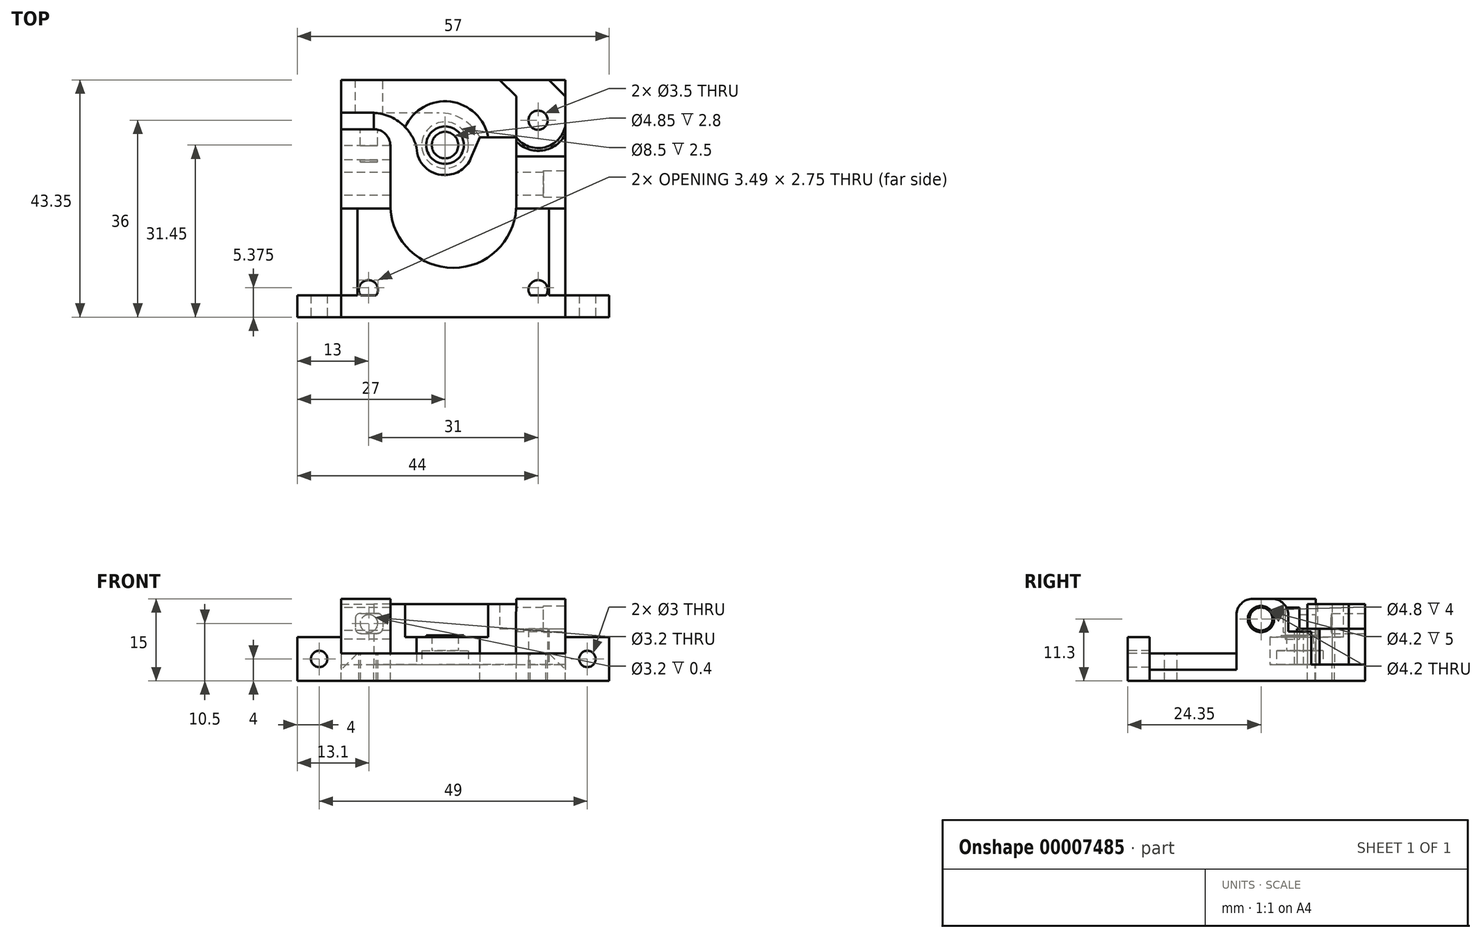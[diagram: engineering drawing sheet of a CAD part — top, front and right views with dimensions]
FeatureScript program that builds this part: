
annotation { "Feature Type Name" : "Feature", "Feature Type Description" : "" }
export const myFeature = defineFeature(function(context is Context, id is Id, definition is map)
    precondition{}
    {
        {
            var Q0;
            Q0=qCreatedBy(makeId("Top.planeOp"),FACE);
            var sketch = newSketch(context, id + "F0", { "sketchPlane" : qUnion([Q0])});
            skLineSegment(sketch, "E0.bottom", {"start": v(-15.5, 15.5) * mm, "end": v(15.5, 15.5) * mm, "construction": true});
            skLineSegment(sketch, "E0.top", {"start": v(-15.5, -15.5) * mm, "end": v(15.5, -15.5) * mm, "construction": true});
            skLineSegment(sketch, "E0.left", {"start": v(-15.5, 15.5) * mm, "end": v(-15.5, -15.5) * mm, "construction": true});
            skLineSegment(sketch, "E0.right", {"start": v(15.5, 15.5) * mm, "end": v(15.5, -15.5) * mm, "construction": true});
            skCircle(sketch, "E1", {"center": v(0, 0) * mm, "radius": 11.5 * mm});
            skLineSegment(sketch, "E2", {"start": v(-15.5, 0) * mm, "end": v(0, 0) * mm, "construction": true});
            skLineSegment(sketch, "E3", {"start": v(0, 0) * mm, "end": v(0, 15.5) * mm, "construction": true});
            skLineSegment(sketch, "E4.0", {"start": v(-20.5, 20.5) * mm, "end": v(20.5, 20.5) * mm});
            skLineSegment(sketch, "E4.1", {"start": v(-20.5, 20.5) * mm, "end": v(-20.5, -20.5) * mm});
            skLineSegment(sketch, "E4.2", {"start": v(-20.5, -20.5) * mm, "end": v(20.5, -20.5) * mm});
            skLineSegment(sketch, "E4.3", {"start": v(20.5, 20.5) * mm, "end": v(20.5, -20.5) * mm});
            skCircle(sketch, "E5", {"center": v(15.5, 15.5) * mm, "radius": 1.75 * mm});
            skCircle(sketch, "E6", {"center": v(-15.5, -15.5) * mm, "radius": 1.75 * mm});
            skCircle(sketch, "E7", {"center": v(15.5, -15.5) * mm, "radius": 1.75 * mm});
            skCircle(sketch, "E8", {"center": v(0, 0) * mm, "radius": 3.75 * mm, "construction": true});
            skCircle(sketch, "E9", {"center": v(-1.5, 10.95) * mm, "radius": 7 * mm, "construction": true});
            skLineSegment(sketch, "E10", {"start": v(0, 3.85) * mm, "end": v(-20.5, 3.85) * mm, "construction": true});
            skLineSegment(sketch, "E11.bottom", {"start": v(-11.5, 0) * mm, "end": v(11.5, 0) * mm, "construction": true});
            skLineSegment(sketch, "E11.left", {"start": v(-11.5, 0) * mm, "end": v(-11.5, 10.85) * mm});
            skLineSegment(sketch, "E11.right", {"start": v(11.5, 0) * mm, "end": v(11.5, 8.85) * mm});
            skLineSegment(sketch, "E12", {"start": v(-20.5, 13.85) * mm, "end": v(-14.5, 13.85) * mm});
            skLineSegment(sketch, "E13", {"start": v(11.5, 8.85) * mm, "end": v(20.5, 8.85) * mm});
            skCircle(sketch, "E14", {"center": v(-1.5, 10.95) * mm, "radius": 2.43 * mm});
            skLineSegment(sketch, "E15", {"start": v(-20.5, 16.85) * mm, "end": v(-2.6, 16.85) * mm});
            skLineSegment(sketch, "E16", {"start": v(-20.5, 22.85) * mm, "end": v(20.5, 22.85) * mm});
            skLineSegment(sketch, "E17", {"start": v(-15.5, 0) * mm, "end": v(-20.5, 0) * mm});
            skLineSegment(sketch, "E18", {"start": v(20.5, 0) * mm, "end": v(11.5, 0) * mm});
            skLineSegment(sketch, "E19", {"start": v(-15.5, 0) * mm, "end": v(-11.5, 0) * mm});
            skLineSegment(sketch, "E20", {"start": v(11.5, 8.85) * mm, "end": v(11.5, 12.35) * mm});
            skLineSegment(sketch, "E21", {"start": v(-11.48, -0.65) * mm, "end": v(-20.5, -0.65) * mm});
            skLineSegment(sketch, "E22", {"start": v(11.48, -0.65) * mm, "end": v(20.5, -0.65) * mm});
            skCircle(sketch, "E23", {"center": v(-1.5, 10.95) * mm, "radius": 1.5 * mm});
            skLineSegment(sketch, "E24", {"start": v(-1.68, 5.5) * mm, "end": v(-1.37, 5.5) * mm});
            skLineSegment(sketch, "E25", {"start": v(3.23, 8.53) * mm, "end": v(4.86, 12.35) * mm});
            skPoint(sketch, "E26.visualSharp", {"position": v(-6.13, 5.5) * mm});
            skArc(sketch, "E26.filletArc", {"start": v(-6.68, 10.44) * mm, "mid": v(-5.2, 6.94) * mm, "end": v(-1.68, 5.5) * mm});
            skPoint(sketch, "E27.visualSharp", {"position": v(1.93, 5.5) * mm});
            skArc(sketch, "E27.filletArc", {"start": v(-1.37, 5.5) * mm, "mid": v(1.38, 6.33) * mm, "end": v(3.23, 8.53) * mm});
            skPoint(sketch, "E28.visualSharp", {"position": v(-11.5, 13.85) * mm});
            skArc(sketch, "E28.filletArc", {"start": v(-11.5, 10.85) * mm, "mid": v(-12.38, 12.97) * mm, "end": v(-14.5, 13.85) * mm});
            skLineSegment(sketch, "E29", {"start": v(11.5, 12.35) * mm, "end": v(4.86, 12.35) * mm});
            skLineSegment(sketch, "E30", {"start": v(20.5, 20.5) * mm, "end": v(20.5, 22.85) * mm});
            skLineSegment(sketch, "E31", {"start": v(-20.5, 20.5) * mm, "end": v(-20.5, 22.85) * mm});
            skLineSegment(sketch, "E32", {"start": v(-14.5, 13.85) * mm, "end": v(-14.5, 16.85) * mm});
            skArc(sketch, "E33", {"start": v(11.5, 12.35) * mm, "mid": v(16.7, 10.55) * mm, "end": v(20.5, 14.54) * mm});
            skArc(sketch, "E34.0", {"start": v(11.5, 11.6) * mm, "mid": v(16.36, 9.97) * mm, "end": v(20.5, 13) * mm});
            skArc(sketch, "E35", {"start": v(-6.68, 10.44) * mm, "mid": v(-9.54, 14.93) * mm, "end": v(-14.5, 16.85) * mm});
            skArc(sketch, "E36", {"start": v(4.86, 12.35) * mm, "mid": v(1.76, 15.64) * mm, "end": v(-2.6, 16.85) * mm});
            skSolve(sketch);
        }
        {
            var Q0;
            {var subQ11=sQuery(id+"F0.wireOp",EDGE,"E4.0");Q0=makeQuery(id+"F0.imprint","IMPRINT",FACE,{"disambiguationData":[TD([[makeQuery(id+"F0.imprint","IMPRINT",EDGE,{"derivedFrom":subQ11}),-1.0]])]});}
            var Q1;
            Q1=makeQuery(id+"F0.imprint","IMPRINT",FACE,{"disambiguationData":[TD([[makeQuery(id+"F0.imprint","IMPRINT",EDGE,{"derivedFrom":sQuery(id+"F0.wireOp",EDGE,"E11.right")}),-1.0]])]});
            var Q2;
            {var subQ3=sQuery(id+"F0.wireOp",EDGE,"E4.2");Q2=makeQuery(id+"F0.imprint","IMPRINT",FACE,{"disambiguationData":[TD([[makeQuery(id+"F0.imprint","IMPRINT",EDGE,{"derivedFrom":subQ3}),1.0]])]});}
            var Q3;
            Q3=makeQuery(id+"F0.imprint","IMPRINT",FACE,{"disambiguationData":[TD([[makeQuery(id+"F0.imprint","IMPRINT",EDGE,{"derivedFrom":sQuery(id+"F0.wireOp",EDGE,"E11.left")}),1.0]])]});
            var Q4;
            {var subQ1=sQuery(id+"F0.wireOp",EDGE,"E18");Q4=makeQuery(id+"F0.imprint","IMPRINT",FACE,{"disambiguationData":[TD([[makeQuery(id+"F0.imprint","IMPRINT",EDGE,{"derivedFrom":subQ1}),1.0]])]});}
            var Q5;
            {var subQ2=sQuery(id+"F0.wireOp",EDGE,"E17");Q5=makeQuery(id+"F0.imprint","IMPRINT",FACE,{"disambiguationData":[TD([[makeQuery(id+"F0.imprint","IMPRINT",EDGE,{"derivedFrom":subQ2}),1.0]])]});}
            var Q6;
            {var subQ11=sQuery(id+"F0.wireOp",EDGE,"E4.0");Q6=makeQuery(id+"F0.imprint","IMPRINT",FACE,{"disambiguationData":[TD([[makeQuery(id+"F0.imprint","IMPRINT",EDGE,{"derivedFrom":subQ11}),-1.0]])]});}
            var Q7;
            Q7=makeQuery(id+"F0.imprint","IMPRINT",FACE,{"disambiguationData":[TD([[makeQuery(id+"F0.imprint","IMPRINT",EDGE,{"derivedFrom":sQuery(id+"F0.wireOp",EDGE,"E4.0")}),1.0]])]});
            var Q8;
            {var subQ4=sQuery(id+"F0.wireOp",EDGE,"E12");Q8=makeQuery(id+"F0.imprint","IMPRINT",FACE,{"disambiguationData":[TD([[makeQuery(id+"F0.imprint","IMPRINT",EDGE,{"derivedFrom":subQ4}),1.0]])]});}
            var Q9;
            {var subQ2=sQuery(id+"F0.wireOp",EDGE,"E13");Q9=makeQuery(id+"F0.imprint","IMPRINT",FACE,{"disambiguationData":[TD([[makeQuery(id+"F0.imprint","IMPRINT",EDGE,{"derivedFrom":subQ2}),1.0]])]});}
            var Q10;
            {var subQ1=sQuery(id+"F0.wireOp",EDGE,"E33");Q10=makeQuery(id+"F0.imprint","IMPRINT",FACE,{"disambiguationData":[TD([[makeQuery(id+"F0.imprint","IMPRINT",EDGE,{"derivedFrom":subQ1}),-1.0]])]});}
            extrude(context, id + "F1", {"entities" : qUnion([Q0, Q1, Q2, Q3, Q4, Q5, Q6, Q7, Q8, Q9, Q10]), "oppositeDirection" : true, "depth" : 3 * mm});
        }
        {
            var Q0;
            {var subQ1=sQuery(id+"F0.wireOp",EDGE,"97cd7f3d-8e90-465d-8939-76c9784581d8");Q0=makeQuery(id+"F0.imprint","IMPRINT",FACE,{"disambiguationData":[TD([[makeQuery(id+"F0.imprint","IMPRINT",EDGE,{"derivedFrom":subQ1}),1.0]])]});}
            var Q1;
            {var subQ6=sQuery(id+"F0.wireOp",EDGE,"E4.0");Q1=makeQuery(id+"F0.imprint","IMPRINT",FACE,{"disambiguationData":[TD([[makeQuery(id+"F0.imprint","IMPRINT",EDGE,{"derivedFrom":subQ6}),-1.0]])]});}
            var Q2;
            Q2=makeQuery(id+"F0.imprint","IMPRINT",FACE,{"disambiguationData":[TD([[makeQuery(id+"F0.imprint","IMPRINT",EDGE,{"derivedFrom":sQuery(id+"F0.wireOp",EDGE,"E4.0")}),1.0]])]});
            var Q3;
            {var subQ1=sQuery(id+"F0.wireOp",EDGE,"E1");var subQ5=sQuery(id+"F0.wireOp",EDGE,"E14");var subQ7=makeQuery(id+"F0.imprint","INTERSECT",VERTEX,{"disambiguationData":[OD(1.0)],"derivedFrom":[subQ1,subQ5]});Q3=makeQuery(id+"F0.imprint","IMPRINT",FACE,{"disambiguationData":[TD([[makeQuery(id+"F0.imprint","IMPRINT",EDGE,{"disambiguationData":[TD([[subQ7,-1.0]])],"derivedFrom":subQ1}),1.0]])]});}
            var Q4;
            {var subQ0=sQuery(id+"F0.wireOp",EDGE,"E27.filletArc");Q4=makeQuery(id+"F0.imprint","IMPRINT",FACE,{"disambiguationData":[TD([[makeQuery(id+"F0.imprint","IMPRINT",EDGE,{"derivedFrom":subQ0}),1.0]])]});}
            var Q5;
            {var subQ4=sQuery(id+"F0.wireOp",EDGE,"E35");Q5=makeQuery(id+"F0.imprint","IMPRINT",FACE,{"disambiguationData":[TD([[makeQuery(id+"F0.imprint","IMPRINT",EDGE,{"derivedFrom":subQ4}),-1.0]])]});}
            extrude(context, id + "F2", {"entities" : qUnion([Q0, Q1, Q2, Q3, Q4, Q5]), "depth" : 10 * mm});
        }
        {
            var Q0;
            Q0=makeQuery(id+"F0.imprint","IMPRINT",FACE,{"disambiguationData":[TD([[makeQuery(id+"F0.imprint","IMPRINT",EDGE,{"derivedFrom":sQuery(id+"F0.wireOp",EDGE,"E11.right")}),-1.0]])]});
            var Q1;
            {var subQ1=sQuery(id+"F0.wireOp",EDGE,"E18");Q1=makeQuery(id+"F0.imprint","IMPRINT",FACE,{"disambiguationData":[TD([[makeQuery(id+"F0.imprint","IMPRINT",EDGE,{"derivedFrom":subQ1}),1.0]])]});}
            var Q2;
            {var subQ2=sQuery(id+"F0.wireOp",EDGE,"E17");Q2=makeQuery(id+"F0.imprint","IMPRINT",FACE,{"disambiguationData":[TD([[makeQuery(id+"F0.imprint","IMPRINT",EDGE,{"derivedFrom":subQ2}),1.0]])]});}
            var Q3;
            Q3=makeQuery(id+"F0.imprint","IMPRINT",FACE,{"disambiguationData":[TD([[makeQuery(id+"F0.imprint","IMPRINT",EDGE,{"derivedFrom":sQuery(id+"F0.wireOp",EDGE,"E11.left")}),1.0]])]});
            var Q4;
            Q4=makeQuery(id+"F2.opExtrude","CAP_FACE",FACE,{"disambiguationData":[OSD([sQuery(id+"F0.wireOp",EDGE,"E4.1"),sQuery(id+"F0.wireOp",EDGE,"E4.3"),sQuery(id+"F0.wireOp",EDGE,"E5"),sQuery(id+"F0.wireOp",EDGE,"E14"),sQuery(id+"F0.wireOp",EDGE,"E15"),sQuery(id+"F0.wireOp",EDGE,"E16"),sQuery(id+"F0.wireOp",EDGE,"4d0ce63a-1545-49a6-93f2-0e6cf358bf14"),sQuery(id+"F0.wireOp",EDGE,"E24"),sQuery(id+"F0.wireOp",EDGE,"E25"),sQuery(id+"F0.wireOp",EDGE,"E26.filletArc"),sQuery(id+"F0.wireOp",EDGE,"E27.filletArc"),sQuery(id+"F0.wireOp",EDGE,"E29"),sQuery(id+"F0.wireOp",EDGE,"E30"),sQuery(id+"F0.wireOp",EDGE,"E31"),sQuery(id+"F0.wireOp",EDGE,"E33")])],"isStart":false});
            extrude(context, id + "F3", {"entities" : qUnion([Q0, Q1, Q2, Q3]), "operationType" : NewBodyOperationType.ADD, "endBoundEntity" : qUnion([Q4]), "depth" : 12 * mm});
        }
        {
            var Q0;
            Q0=makeQuery(id+"F2.opExtrude","CAP_FACE",FACE,{"disambiguationData":[OSD([sQuery(id+"F0.wireOp",EDGE,"E4.1"),sQuery(id+"F0.wireOp",EDGE,"E4.3"),sQuery(id+"F0.wireOp",EDGE,"E5"),sQuery(id+"F0.wireOp",EDGE,"E14"),sQuery(id+"F0.wireOp",EDGE,"E15"),sQuery(id+"F0.wireOp",EDGE,"E16"),sQuery(id+"F0.wireOp",EDGE,"4d0ce63a-1545-49a6-93f2-0e6cf358bf14"),sQuery(id+"F0.wireOp",EDGE,"E24"),sQuery(id+"F0.wireOp",EDGE,"E25"),sQuery(id+"F0.wireOp",EDGE,"E26.filletArc"),sQuery(id+"F0.wireOp",EDGE,"E27.filletArc"),sQuery(id+"F0.wireOp",EDGE,"E29"),sQuery(id+"F0.wireOp",EDGE,"E30"),sQuery(id+"F0.wireOp",EDGE,"E31"),sQuery(id+"F0.wireOp",EDGE,"E33")])],"isStart":false});
            var sketch = newSketch(context, id + "F4", { "sketchPlane" : qUnion([Q0])});
            skLineSegment(sketch, "E37.0", {"start": v(11.5, 8.85) * mm, "end": v(20.5, 8.85) * mm});
            skCircle(sketch, "E38.0", {"center": v(-1.5, 10.95) * mm, "radius": 7 * mm});
            skCircle(sketch, "E38.1", {"center": v(-1.5, 10.95) * mm, "radius": 2.43 * mm});
            skCircle(sketch, "E39.0", {"center": v(-1.5, 10.95) * mm, "radius": 8 * mm});
            skSolve(sketch);
        }
        {
            var Q0;
            Q0=makeQuery(id+"F4.imprint","IMPRINT",FACE,{"disambiguationData":[TD([[makeQuery(id+"F4.imprint","IMPRINT",EDGE,{"derivedFrom":sQuery(id+"F4.wireOp",EDGE,"E38.1")}),-1.0]])]});
            var Q1;
            {var subQ0=makeQuery(id+"F2.opExtrude","CAP_EDGE",EDGE,{"disambiguationData":[OSD([sQuery(id+"F0.wireOp",EDGE,"E16")])],"isStart":false});var subQ1=sQuery(id+"F4.wireOp",EDGE,"E38.0");var subQ2=makeQuery(id+"F4.imprint","INTERSECT",VERTEX,{"disambiguationData":[OD(1.0)],"derivedFrom":[subQ0,subQ1]});Q1=makeQuery(id+"F4.imprint","IMPRINT",FACE,{"disambiguationData":[TD([[makeQuery(id+"F4.imprint","IMPRINT",EDGE,{"disambiguationData":[TD([[subQ2,1.0]])],"derivedFrom":subQ1}),-1.0]])]});}
            var Q2;
            {var subQ0=makeQuery(id+"F2.opExtrude","CAP_EDGE",EDGE,{"disambiguationData":[OSD([sQuery(id+"F0.wireOp",EDGE,"E16")])],"isStart":false});var subQ1=sQuery(id+"F4.wireOp",EDGE,"E38.0");var subQ2=makeQuery(id+"F4.imprint","INTERSECT",VERTEX,{"disambiguationData":[OD(0.0)],"derivedFrom":[subQ0,subQ1]});Q2=makeQuery(id+"F4.imprint","IMPRINT",FACE,{"disambiguationData":[TD([[makeQuery(id+"F4.imprint","IMPRINT",EDGE,{"disambiguationData":[TD([[subQ2,-1.0]])],"derivedFrom":subQ1}),-1.0]])]});}
            extrude(context, id + "F5", {"entities" : qUnion([Q0, Q1, Q2]), "operationType" : NewBodyOperationType.REMOVE, "oppositeDirection" : true, "depth" : 5 * mm});
        }
        {
            var Q0;
            {var subQ0=sQuery(id+"F0.wireOp",EDGE,"E4.3");Q0=makeQuery(id+"F2.boolean.opBoolean","MERGE",FACE,{"derivedFrom":[makeQuery(id+"F1.opExtrude","SWEPT_FACE",FACE,{"disambiguationData":[OSD([subQ0])]}),makeQuery(id+"F2.opExtrude","SWEPT_FACE",FACE,{"disambiguationData":[OSD([subQ0])]})]});}
            var sketch = newSketch(context, id + "F6", { "sketchPlane" : qUnion([Q0])});
            skCircle(sketch, "E40", {"center": v(3.85, 8.3) * mm, "radius": 1.5 * mm});
            skPoint(sketch, "E41.0", {"position": v(3.85, 0) * mm});
            skLineSegment(sketch, "E42.0", {"start": v(8.53, 5) * mm, "end": v(13.38, 5) * mm});
            skSolve(sketch);
        }
        {
            var Q0;
            Q0=makeQuery(id+"F6.imprint","IMPRINT",FACE,{"disambiguationData":[TD([[makeQuery(id+"F6.imprint","IMPRINT",EDGE,{"derivedFrom":sQuery(id+"F6.wireOp",EDGE,"E40")}),1.0]])]});
            extrude(context, id + "F7", {"entities" : qUnion([Q0]), "operationType" : NewBodyOperationType.REMOVE, "oppositeDirection" : true, "depth" : 50 * mm});
        }
        {
            var Q0;
            Q0=makeQuery(id+"F2.opExtrude","SWEPT_FACE",FACE,{"disambiguationData":[OSD([sQuery(id+"F0.wireOp",EDGE,"E16")])]});
            var sketch = newSketch(context, id + "F8", { "sketchPlane" : qUnion([Q0])});
            skLineSegment(sketch, "E43", {"start": v(15.4, 10) * mm, "end": v(15.4, 7.5) * mm, "construction": true});
            skCircle(sketch, "E44", {"center": v(15.4, 7.5) * mm, "radius": 1.6 * mm});
            skLineSegment(sketch, "E45.0", {"start": v(-0.93, 5) * mm, "end": v(3.92, 5) * mm, "construction": true});
            skLineSegment(sketch, "E46", {"start": v(3.92, 5) * mm, "end": v(3.92, 10) * mm, "construction": true});
            skLineSegment(sketch, "E47", {"start": v(3.92, 10) * mm, "end": v(3.92, 7.5) * mm, "construction": true});
            skLineSegment(sketch, "E48", {"start": v(3.92, 7.5) * mm, "end": v(15.4, 7.5) * mm, "construction": true});
            skSolve(sketch);
        }
        {
            var Q0;
            Q0=makeQuery(id+"F8.imprint","IMPRINT",FACE,{"disambiguationData":[TD([[makeQuery(id+"F8.imprint","IMPRINT",EDGE,{"derivedFrom":sQuery(id+"F8.wireOp",EDGE,"E44")}),1.0]])]});
            var Q1;
            Q1=sQuery(id+"F8.wireOp",EDGE,"E44");
            extrude(context, id + "F9", {"entities" : qUnion([Q0]), "operationType" : NewBodyOperationType.REMOVE, "surfaceEntities" : qUnion([Q1]), "oppositeDirection" : true, "depth" : 15 * mm});
        }
        {
            var Q0;
            {var subQ0=sQuery(id+"F0.wireOp",EDGE,"E4.1");var subQ1=makeQuery(id+"F0.imprint","INTERSECT",VERTEX,{"derivedFrom":[subQ0,sQuery(id+"F0.wireOp",EDGE,"E17")]});var subQ2=makeQuery(id+"F0.imprint","IMPRINT",EDGE,{"disambiguationData":[TD([[makeQuery(id+"F0.imprint","INTERSECT",VERTEX,{"derivedFrom":[subQ0,sQuery(id+"F0.wireOp",EDGE,"E12")]}),-1.0]])],"derivedFrom":subQ0});var subQ4=makeQuery(id+"F0.imprint","IMPRINT",EDGE,{"disambiguationData":[TD([[subQ1,-1.0]])],"derivedFrom":subQ0});Q0=makeQuery(id+"F2.boolean.opBoolean","MERGE",FACE,{"derivedFrom":[makeQuery(id+"F1.opExtrude","SWEPT_FACE",FACE,{"disambiguationData":[OSD([subQ0]),TDD([subQ2,subQ4,makeQuery(id+"F0.imprint","IMPRINT",EDGE,{"disambiguationData":[TD([[makeQuery(id+"F0.imprint","INTERSECT",VERTEX,{"derivedFrom":[subQ0,sQuery(id+"F0.wireOp",EDGE,"E4.2")]}),1.0]])],"derivedFrom":subQ0})])]}),makeQuery(id+"F2.opExtrude","SWEPT_FACE",FACE,{"disambiguationData":[OSD([subQ0]),TDD([subQ2,subQ4])]})]});}
            var sketch = newSketch(context, id + "F10", { "sketchPlane" : qUnion([Q0])});
            skLineSegment(sketch, "E49", {"start": v(-22.85, 7.5) * mm, "end": v(-9.55, 7.5) * mm});
            skLineSegment(sketch, "E50.rect.bottom", {"start": v(-8.25, 10.4) * mm, "end": v(-10.85, 10.4) * mm});
            skLineSegment(sketch, "E50.rect.top", {"start": v(-8.25, 4.6) * mm, "end": v(-10.85, 4.6) * mm});
            skLineSegment(sketch, "E50.rect.left", {"start": v(-8.25, 10.4) * mm, "end": v(-8.25, 4.6) * mm});
            skLineSegment(sketch, "E50.rect.right", {"start": v(-10.85, 10.4) * mm, "end": v(-10.85, 4.6) * mm});
            skPoint(sketch, "E50.rect.middle", {"position": v(-9.55, 7.5) * mm});
            skLineSegment(sketch, "E51.0", {"start": v(-22.85, 5.9) * mm, "end": v(-22.85, 9.1) * mm});
            skSolve(sketch);
        }
        {
            var Q0;
            {var subQ3=sQuery(id+"F10.wireOp",EDGE,"E50.rect.bottom");Q0=makeQuery(id+"F10.imprint","IMPRINT",FACE,{"disambiguationData":[TD([[makeQuery(id+"F10.imprint","IMPRINT",EDGE,{"derivedFrom":subQ3}),1.0]])]});}
            extrude(context, id + "F11", {"entities" : qUnion([Q0]), "operationType" : NewBodyOperationType.REMOVE, "oppositeDirection" : true, "depth" : 9 * mm});
        }
        {
            var Q0;
            Q0=makeQuery(id+"F2.opExtrude","SWEPT_FACE",FACE,{"disambiguationData":[OSD([sQuery(id+"F0.wireOp",EDGE,"E16")])]});
            var sketch = newSketch(context, id + "F12", { "sketchPlane" : qUnion([Q0])});
            skCircle(sketch, "E52.0", {"center": v(15.4, 7.5) * mm, "radius": 1.6 * mm});
            skLineSegment(sketch, "E53.rect.bottom", {"start": v(16.9, 9.34) * mm, "end": v(13.9, 9.34) * mm});
            skLineSegment(sketch, "E53.rect.top", {"start": v(16.9, 5.66) * mm, "end": v(13.9, 5.66) * mm});
            skLineSegment(sketch, "E53.rect.left", {"start": v(17.9, 8.34) * mm, "end": v(17.9, 6.66) * mm});
            skLineSegment(sketch, "E53.rect.right", {"start": v(12.9, 8.34) * mm, "end": v(12.9, 6.66) * mm});
            skPoint(sketch, "E54.visualSharp", {"position": v(17.9, 9.34) * mm});
            skArc(sketch, "E54.filletArc", {"start": v(17.9, 8.34) * mm, "mid": v(17.62, 9.05) * mm, "end": v(16.9, 9.34) * mm});
            skPoint(sketch, "E55.visualSharp", {"position": v(17.9, 5.66) * mm});
            skArc(sketch, "E55.filletArc", {"start": v(16.9, 5.66) * mm, "mid": v(17.62, 5.95) * mm, "end": v(17.9, 6.66) * mm});
            skPoint(sketch, "E56.visualSharp", {"position": v(12.9, 5.66) * mm});
            skArc(sketch, "E56.filletArc", {"start": v(12.9, 6.66) * mm, "mid": v(13.18, 5.95) * mm, "end": v(13.9, 5.66) * mm});
            skPoint(sketch, "E57.visualSharp", {"position": v(12.9, 9.34) * mm});
            skArc(sketch, "E57.filletArc", {"start": v(13.9, 9.34) * mm, "mid": v(13.18, 9.05) * mm, "end": v(12.9, 8.34) * mm});
            skSolve(sketch);
        }
        {
            var Q0;
            Q0=makeQuery(id+"F12.imprint","IMPRINT",FACE,{"disambiguationData":[TD([[makeQuery(id+"F12.imprint","IMPRINT",EDGE,{"derivedFrom":sQuery(id+"F12.wireOp",EDGE,"E52.0")}),-1.0]])]});
            extrude(context, id + "F13", {"entities" : qUnion([Q0]), "operationType" : NewBodyOperationType.REMOVE, "endBound" : BoundingType.UP_TO_NEXT, "oppositeDirection" : true, "depth" : 5 * mm});
        }
        {
            var Q0;
            {var subQ0=sQuery(id+"F0.wireOp",EDGE,"E4.3");Q0=makeQuery(id+"F2.boolean.opBoolean","MERGE",FACE,{"derivedFrom":[makeQuery(id+"F1.opExtrude","SWEPT_FACE",FACE,{"disambiguationData":[OSD([subQ0])]}),makeQuery(id+"F2.opExtrude","SWEPT_FACE",FACE,{"disambiguationData":[OSD([subQ0])]})]});}
            var sketch = newSketch(context, id + "F14", { "sketchPlane" : qUnion([Q0])});
            skCircle(sketch, "E58.0", {"center": v(3.85, 8.3) * mm, "radius": 1.5 * mm});
            skCircle(sketch, "E59", {"center": v(3.85, 8.3) * mm, "radius": 2.4 * mm});
            skSolve(sketch);
        }
        {
            var Q0;
            Q0=makeQuery(id+"F14.imprint","IMPRINT",FACE,{"disambiguationData":[TD([[makeQuery(id+"F14.imprint","IMPRINT",EDGE,{"derivedFrom":sQuery(id+"F14.wireOp",EDGE,"E58.0")}),-1.0]])]});
            extrude(context, id + "F15", {"entities" : qUnion([Q0]), "operationType" : NewBodyOperationType.REMOVE, "oppositeDirection" : true, "depth" : 4 * mm});
        }
        {
            var Q0;
            {var subQ0=sQuery(id+"F0.wireOp",EDGE,"E4.1");var subQ1=makeQuery(id+"F0.imprint","INTERSECT",VERTEX,{"derivedFrom":[subQ0,sQuery(id+"F0.wireOp",EDGE,"E17")]});var subQ2=makeQuery(id+"F0.imprint","IMPRINT",EDGE,{"disambiguationData":[TD([[makeQuery(id+"F0.imprint","INTERSECT",VERTEX,{"derivedFrom":[subQ0,sQuery(id+"F0.wireOp",EDGE,"E12")]}),-1.0]])],"derivedFrom":subQ0});var subQ4=makeQuery(id+"F0.imprint","IMPRINT",EDGE,{"disambiguationData":[TD([[subQ1,-1.0]])],"derivedFrom":subQ0});Q0=makeQuery(id+"F2.boolean.opBoolean","MERGE",FACE,{"derivedFrom":[makeQuery(id+"F1.opExtrude","SWEPT_FACE",FACE,{"disambiguationData":[OSD([subQ0]),TDD([subQ2,subQ4,makeQuery(id+"F0.imprint","IMPRINT",EDGE,{"disambiguationData":[TD([[makeQuery(id+"F0.imprint","INTERSECT",VERTEX,{"derivedFrom":[subQ0,sQuery(id+"F0.wireOp",EDGE,"E4.2")]}),1.0]])],"derivedFrom":subQ0})])]}),makeQuery(id+"F2.opExtrude","SWEPT_FACE",FACE,{"disambiguationData":[OSD([subQ0]),TDD([subQ2,subQ4])]})]});}
            var sketch = newSketch(context, id + "F16", { "sketchPlane" : qUnion([Q0])});
            skCircle(sketch, "E60.0", {"center": v(-3.85, 8.3) * mm, "radius": 1.5 * mm});
            skCircle(sketch, "E61", {"center": v(-3.85, 8.3) * mm, "radius": 2.1 * mm});
            skSolve(sketch);
        }
        {
            var Q0;
            Q0=makeQuery(id+"F16.imprint","IMPRINT",FACE,{"disambiguationData":[TD([[makeQuery(id+"F16.imprint","IMPRINT",EDGE,{"derivedFrom":sQuery(id+"F16.wireOp",EDGE,"E60.0")}),-1.0]])]});
            var Q1;
            Q1=sQuery(id+"F16.wireOp",EDGE,"E61");
            extrude(context, id + "F17", {"entities" : qUnion([Q0]), "operationType" : NewBodyOperationType.REMOVE, "surfaceEntities" : qUnion([Q1]), "oppositeDirection" : true, "depth" : 46.76 * mm});
        }
        {
            var Q0;
            {var subQ0=sQuery(id+"F0.wireOp",EDGE,"E4.0");var subQ1=sQuery(id+"F0.wireOp",EDGE,"E15");var subQ2=sQuery(id+"F0.wireOp",EDGE,"4d0ce63a-1545-49a6-93f2-0e6cf358bf14");var subQ3=sQuery(id+"F0.wireOp",EDGE,"E24");var subQ4=sQuery(id+"F0.wireOp",EDGE,"E25");var subQ5=sQuery(id+"F0.wireOp",EDGE,"E26.filletArc");var subQ6=sQuery(id+"F0.wireOp",EDGE,"E27.filletArc");var subQ7=sQuery(id+"F4.wireOp",EDGE,"E38.0");var subQ8=sQuery(id+"F4.wireOp",EDGE,"E38.1");var subQ9=sQuery(id+"F4.wireOp",EDGE,"E39.0");Q0=makeQuery(id+"FuloRg8u4kZyhOY_7.boolean.opBoolean","MERGE",FACE,{"derivedFrom":[makeQuery(id+"F5.boolean.opBoolean","COPY",FACE,{"derivedFrom":makeQuery(id+"F5.opExtrude","CAP_FACE",FACE,{"disambiguationData":[OSD([subQ0,subQ1,subQ2,subQ3,subQ4,subQ5,subQ6,subQ7,subQ8,subQ9])],"isStart":false})}),makeQuery(id+"FuloRg8u4kZyhOY_7.opExtrude","SWEPT_FACE",FACE,{"disambiguationData":[OSD([subQ0,subQ1,subQ2,subQ3,subQ4,subQ5,subQ6,subQ7,subQ8,subQ9])]})]});}
            var sketch = newSketch(context, id + "F18", { "sketchPlane" : qUnion([Q0])});
            skCircle(sketch, "E62.0", {"center": v(-1.5, 10.95) * mm, "radius": 3.43 * mm});
            skSolve(sketch);
        }
        {
            var Q0;
            Q0=makeQuery(id+"F18.imprint","IMPRINT",FACE,{"disambiguationData":[TD([[makeQuery(id+"F18.imprint","IMPRINT",EDGE,{"derivedFrom":sQuery(id+"F18.wireOp",EDGE,"E62.0")}),1.0]])]});
            extrude(context, id + "F19", {"entities" : qUnion([Q0]), "operationType" : NewBodyOperationType.ADD, "depth" : 0.3 * mm});
        }
        {
            var Q0;
            Q0=makeQuery(id+"F1.opExtrude","SWEPT_FACE",FACE,{"disambiguationData":[OSD([sQuery(id+"F0.wireOp",EDGE,"E4.2")])]});
            var sketch = newSketch(context, id + "F20", { "sketchPlane" : qUnion([Q0])});
            skLineSegment(sketch, "E63.bottom", {"start": v(20.5, -3) * mm, "end": v(28.5, -3) * mm});
            skLineSegment(sketch, "E63.top", {"start": v(20.5, 5) * mm, "end": v(28.5, 5) * mm});
            skLineSegment(sketch, "E63.left", {"start": v(20.5, -3) * mm, "end": v(20.5, 5) * mm});
            skLineSegment(sketch, "E63.right", {"start": v(28.5, -3) * mm, "end": v(28.5, 5) * mm});
            skLineSegment(sketch, "E64.bottom", {"start": v(-20.5, -3) * mm, "end": v(-28.5, -3) * mm});
            skLineSegment(sketch, "E64.top", {"start": v(-20.5, 5) * mm, "end": v(-28.5, 5) * mm});
            skLineSegment(sketch, "E64.left", {"start": v(-20.5, -3) * mm, "end": v(-20.5, 5) * mm});
            skLineSegment(sketch, "E64.right", {"start": v(-28.5, -3) * mm, "end": v(-28.5, 5) * mm});
            skLineSegment(sketch, "E65", {"start": v(-28.5, 1) * mm, "end": v(-20.5, 1) * mm, "construction": true});
            skLineSegment(sketch, "E66", {"start": v(20.5, 1) * mm, "end": v(28.5, 1) * mm, "construction": true});
            skCircle(sketch, "E67", {"center": v(-24.5, 1) * mm, "radius": 1.5 * mm});
            skCircle(sketch, "E68", {"center": v(24.5, 1) * mm, "radius": 1.5 * mm});
            skSolve(sketch);
        }
        {
            var Q0;
            {var subQ4=sQuery(id+"F20.wireOp",EDGE,"E64.bottom");Q0=makeQuery(id+"F20.imprint","IMPRINT",FACE,{"disambiguationData":[TD([[makeQuery(id+"F20.imprint","IMPRINT",EDGE,{"derivedFrom":subQ4}),-1.0]])]});}
            var Q1;
            {var subQ0=sQuery(id+"F0.wireOp",EDGE,"E4.2");var subQ2=makeQuery(id+"F1.opExtrude","CAP_EDGE",EDGE,{"disambiguationData":[OSD([subQ0])],"isStart":true});Q1=makeQuery(id+"F20.imprint","IMPRINT",FACE,{"disambiguationData":[TD([[makeQuery(id+"F20.imprint","IMPRINT",EDGE,{"derivedFrom":subQ2}),-1.0]])]});}
            var Q2;
            {var subQ4=sQuery(id+"F20.wireOp",EDGE,"E63.bottom");Q2=makeQuery(id+"F20.imprint","IMPRINT",FACE,{"disambiguationData":[TD([[makeQuery(id+"F20.imprint","IMPRINT",EDGE,{"derivedFrom":subQ4}),1.0]])]});}
            extrude(context, id + "F21", {"entities" : qUnion([Q0, Q1, Q2]), "operationType" : NewBodyOperationType.ADD, "oppositeDirection" : true, "depth" : 4 * mm});
        }
        {
            var Q0;
            {var subQ0=sQuery(id+"F0.wireOp",EDGE,"E1");var subQ1=sQuery(id+"F0.wireOp",EDGE,"E4.1");var subQ2=sQuery(id+"F0.wireOp",EDGE,"E4.2");var subQ3=sQuery(id+"F0.wireOp",EDGE,"E4.3");var subQ4=sQuery(id+"F0.wireOp",EDGE,"E6");var subQ5=sQuery(id+"F0.wireOp",EDGE,"E7");var subQ6=sQuery(id+"F0.wireOp",EDGE,"E11.left");var subQ7=sQuery(id+"F0.wireOp",EDGE,"E11.right");var subQ8=sQuery(id+"F0.wireOp",EDGE,"E30");var subQ9=sQuery(id+"F0.wireOp",EDGE,"E31");Q0=makeQuery(id+"F3.boolean.opBoolean","SPLIT",FACE,{"disambiguationData":[TD([makeQuery(id+"F1.opExtrude","SWEPT_FACE",FACE,{"disambiguationData":[OSD([subQ0])]})])],"derivedFrom":makeQuery(id+"F1.opExtrude","CAP_FACE",FACE,{"disambiguationData":[OSD([subQ0,subQ1,subQ2,subQ3,sQuery(id+"F0.wireOp",EDGE,"E5"),subQ4,subQ5,subQ6,subQ7,sQuery(id+"F0.wireOp",EDGE,"E14"),sQuery(id+"F0.wireOp",EDGE,"E15"),sQuery(id+"F0.wireOp",EDGE,"E16"),sQuery(id+"F0.wireOp",EDGE,"E20"),sQuery(id+"F0.wireOp",EDGE,"E28.filletArc"),sQuery(id+"F0.wireOp",EDGE,"E29"),subQ8,subQ9,sQuery(id+"F0.wireOp",EDGE,"E32"),sQuery(id+"F0.wireOp",EDGE,"97cd7f3d-8e90-465d-8939-76c9784581d8")])],"isStart":true})});}
            extrude(context, id + "F22", {"entities" : qUnion([Q0]), "operationType" : NewBodyOperationType.ADD, "depth" : 2 * mm});
        }
        {
            var Q0;
            Q0=makeQuery(id+"F3.opExtrude","CAP_EDGE",EDGE,{"disambiguationData":[OSD([sQuery(id+"F0.wireOp",EDGE,"E21")])],"isStart":true});
            var Q1;
            Q1=makeQuery(id+"F3.opExtrude","CAP_EDGE",EDGE,{"disambiguationData":[OSD([sQuery(id+"F0.wireOp",EDGE,"E22")])],"isStart":true});
            var Q2;
            Q2=makeQuery(id+"F3.opExtrude","CAP_EDGE",EDGE,{"disambiguationData":[OSD([sQuery(id+"F0.wireOp",EDGE,"E22")])],"isStart":false});
            var Q3;
            Q3=makeQuery(id+"F3.opExtrude","CAP_EDGE",EDGE,{"disambiguationData":[OSD([sQuery(id+"F0.wireOp",EDGE,"E21")])],"isStart":false});
            var Q4;
            Q4=makeQuery(id+"F21.opExtrude","SWEPT_EDGE",EDGE,{"disambiguationData":[OSD([sQuery(id+"F0.wireOp",EDGE,"E4.2"),sQuery(id+"F20.wireOp",EDGE,"E64.left")])]});
            var Q5;
            Q5=makeQuery(id+"F21.opExtrude","SWEPT_EDGE",EDGE,{"disambiguationData":[OSD([sQuery(id+"F0.wireOp",EDGE,"E4.2"),sQuery(id+"F20.wireOp",EDGE,"E63.left")])]});
            var Q6;
            Q6=makeQuery(id+"F3.opExtrude","CAP_EDGE",EDGE,{"disambiguationData":[OSD([sQuery(id+"F0.wireOp",EDGE,"E13")])],"isStart":false});
            var Q7;
            Q7=makeQuery(id+"F22.opExtrude","CAP_EDGE",EDGE,{"disambiguationData":[OSD([sQuery(id+"F0.wireOp",EDGE,"E21")])],"isStart":false});
            var Q8;
            Q8=makeQuery(id+"F22.opExtrude","CAP_EDGE",EDGE,{"disambiguationData":[OSD([sQuery(id+"F0.wireOp",EDGE,"E22")])],"isStart":false});
            fillet(context, id + "F23", {"entities" : qUnion([Q0, Q1, Q2, Q3, Q4, Q5, Q6, Q7, Q8]), "radius" : 3 * mm, "tangentPropagation" : true, "allowEdgeOverflow" : false});
        }
        {
            var Q0;
            Q0=makeQuery(id+"F2.opExtrude","CAP_FACE",FACE,{"disambiguationData":[OSD([sQuery(id+"F0.wireOp",EDGE,"E4.1"),sQuery(id+"F0.wireOp",EDGE,"E4.3"),sQuery(id+"F0.wireOp",EDGE,"E5"),sQuery(id+"F0.wireOp",EDGE,"E14"),sQuery(id+"F0.wireOp",EDGE,"E15"),sQuery(id+"F0.wireOp",EDGE,"E16"),sQuery(id+"F0.wireOp",EDGE,"E24"),sQuery(id+"F0.wireOp",EDGE,"E25"),sQuery(id+"F0.wireOp",EDGE,"E26.filletArc"),sQuery(id+"F0.wireOp",EDGE,"E27.filletArc"),sQuery(id+"F0.wireOp",EDGE,"E29"),sQuery(id+"F0.wireOp",EDGE,"E30"),sQuery(id+"F0.wireOp",EDGE,"E31"),sQuery(id+"F0.wireOp",EDGE,"E33"),sQuery(id+"F0.wireOp",EDGE,"E35")])],"isStart":false});
            var sketch = newSketch(context, id + "F24", { "sketchPlane" : qUnion([Q0])});
            skLineSegment(sketch, "E69", {"start": v(11.5, 12.35) * mm, "end": v(11.5, 22.85) * mm});
            skArc(sketch, "E70.0", {"start": v(11.5, 12.35) * mm, "mid": v(16.7, 10.55) * mm, "end": v(20.5, 14.54) * mm});
            skLineSegment(sketch, "E71.0", {"start": v(20.5, 22.85) * mm, "end": v(20.5, 14.54) * mm});
            skLineSegment(sketch, "E72.0", {"start": v(-20.5, 22.85) * mm, "end": v(20.5, 22.85) * mm});
            skSolve(sketch);
        }
        {
            var Q0;
            {var subQ1=sQuery(id+"F24.wireOp",EDGE,"E69");Q0=makeQuery(id+"F24.imprint","IMPRINT",FACE,{"disambiguationData":[TD([[makeQuery(id+"F24.imprint","IMPRINT",EDGE,{"derivedFrom":subQ1}),-1.0]])]});}
            extrude(context, id + "F25", {"entities" : qUnion([Q0]), "operationType" : NewBodyOperationType.REMOVE, "oppositeDirection" : true, "depth" : 3.5 * mm});
        }
        {
            var Q0;
            {var subQ2=sQuery(id+"F0.wireOp",EDGE,"E13");Q0=makeQuery(id+"F0.imprint","IMPRINT",FACE,{"disambiguationData":[TD([[makeQuery(id+"F0.imprint","IMPRINT",EDGE,{"derivedFrom":subQ2}),1.0]])]});}
            extrude(context, id + "F26", {"entities" : qUnion([Q0]), "operationType" : NewBodyOperationType.ADD, "depth" : 6 * mm});
        }
        {
            var Q0;
            {var subQ0=sQuery(id+"F0.wireOp",EDGE,"E4.1");var subQ1=sQuery(id+"F0.wireOp",EDGE,"E15");var subQ2=sQuery(id+"F0.wireOp",EDGE,"E16");var subQ3=sQuery(id+"F0.wireOp",EDGE,"E31");var subQ4=sQuery(id+"F0.wireOp",EDGE,"E35");Q0=makeQuery(id+"F5.boolean.opBoolean","SPLIT",FACE,{"disambiguationData":[TD([makeQuery(id+"F2.opExtrude","SWEPT_FACE",FACE,{"disambiguationData":[OSD([subQ1])]})])],"derivedFrom":makeQuery(id+"F2.opExtrude","CAP_FACE",FACE,{"disambiguationData":[OSD([subQ0,sQuery(id+"F0.wireOp",EDGE,"E4.3"),sQuery(id+"F0.wireOp",EDGE,"E5"),sQuery(id+"F0.wireOp",EDGE,"E14"),subQ1,subQ2,sQuery(id+"F0.wireOp",EDGE,"E24"),sQuery(id+"F0.wireOp",EDGE,"E25"),sQuery(id+"F0.wireOp",EDGE,"E26.filletArc"),sQuery(id+"F0.wireOp",EDGE,"E27.filletArc"),sQuery(id+"F0.wireOp",EDGE,"E29"),sQuery(id+"F0.wireOp",EDGE,"E30"),subQ3,sQuery(id+"F0.wireOp",EDGE,"E33"),subQ4])],"isStart":false})});}
            extrude(context, id + "F27", {"entities" : qUnion([Q0]), "operationType" : NewBodyOperationType.ADD, "depth" : 1 * mm});
        }
        {
            var Q0;
            Q0=makeQuery(id+"F2.opExtrude","CAP_FACE",FACE,{"disambiguationData":[OSD([sQuery(id+"F0.wireOp",EDGE,"E4.1"),sQuery(id+"F0.wireOp",EDGE,"E4.3"),sQuery(id+"F0.wireOp",EDGE,"E5"),sQuery(id+"F0.wireOp",EDGE,"E14"),sQuery(id+"F0.wireOp",EDGE,"E15"),sQuery(id+"F0.wireOp",EDGE,"E16"),sQuery(id+"F0.wireOp",EDGE,"E24"),sQuery(id+"F0.wireOp",EDGE,"E25"),sQuery(id+"F0.wireOp",EDGE,"E26.filletArc"),sQuery(id+"F0.wireOp",EDGE,"E27.filletArc"),sQuery(id+"F0.wireOp",EDGE,"E29"),sQuery(id+"F0.wireOp",EDGE,"E30"),sQuery(id+"F0.wireOp",EDGE,"E31"),sQuery(id+"F0.wireOp",EDGE,"E33"),sQuery(id+"F0.wireOp",EDGE,"E35")])],"isStart":true});
            var sketch = newSketch(context, id + "F28", { "sketchPlane" : qUnion([Q0])});
            skCircle(sketch, "E73", {"center": v(-1.5, -10.95) * mm, "radius": 4.25 * mm});
            skSolve(sketch);
        }
        {
            var Q0;
            Q0=makeQuery(id+"F28.imprint","IMPRINT",FACE,{"disambiguationData":[TD([[makeQuery(id+"F28.imprint","IMPRINT",EDGE,{"derivedFrom":sQuery(id+"F28.wireOp",EDGE,"E73")}),1.0]])]});
            extrude(context, id + "F29", {"entities" : qUnion([Q0]), "operationType" : NewBodyOperationType.REMOVE, "oppositeDirection" : true, "depth" : 2.5 * mm});
        }
        {
            var Q0;
            {var subQ0=sQuery(id+"F0.wireOp",EDGE,"E4.2");var subQ1=sQuery(id+"F0.wireOp",EDGE,"E4.3");var subQ2=sQuery(id+"F0.wireOp",EDGE,"E30");var subQ3=sQuery(id+"F20.wireOp",EDGE,"E63.left");Q0=makeQuery(id+"F22.boolean.opBoolean","SPLIT",EDGE,{"disambiguationData":[TD([makeQuery(id+"F1.opExtrude","SWEPT_FACE",FACE,{"disambiguationData":[OSD([subQ0])]})])],"derivedFrom":makeQuery(id+"F22.opExtrude","CAP_EDGE",EDGE,{"disambiguationData":[OSD([subQ0,subQ1,subQ2,subQ3])],"isStart":false})});}
            var Q1;
            {var subQ0=sQuery(id+"F0.wireOp",EDGE,"E4.1");var subQ1=sQuery(id+"F0.wireOp",EDGE,"E4.2");var subQ2=sQuery(id+"F0.wireOp",EDGE,"E31");var subQ3=sQuery(id+"F20.wireOp",EDGE,"E64.left");Q1=makeQuery(id+"F22.boolean.opBoolean","SPLIT",EDGE,{"disambiguationData":[TD([makeQuery(id+"F1.opExtrude","SWEPT_FACE",FACE,{"disambiguationData":[OSD([subQ1])]})])],"derivedFrom":makeQuery(id+"F22.opExtrude","CAP_EDGE",EDGE,{"disambiguationData":[OSD([subQ0,subQ1,subQ2,subQ3])],"isStart":false})});}
            var Q2;
            Q2=makeQuery(id+"F2.opExtrude","SWEPT_EDGE",EDGE,{"disambiguationData":[OSD([sQuery(id+"F0.wireOp",EDGE,"E16"),sQuery(id+"F0.wireOp",EDGE,"E30")])]});
            var Q3;
            {var subQ0=sQuery(id+"F24.wireOp",EDGE,"E69");var subQ1=sQuery(id+"F24.wireOp",EDGE,"E72.0");Q3=makeQuery(id+"F27.boolean.opBoolean","MERGE",EDGE,{"derivedFrom":[makeQuery(id+"F25.boolean.opBoolean","COPY",EDGE,{"derivedFrom":makeQuery(id+"F25.opExtrude","SWEPT_EDGE",EDGE,{"disambiguationData":[OSD([subQ0,subQ1])]})}),makeQuery(id+"F27.opExtrude","SWEPT_EDGE",EDGE,{"disambiguationData":[OSD([subQ0,subQ1])]})]});}
            chamfer(context, id + "F30", {"entities" : qUnion([Q0, Q1, Q2, Q3]), "width" : 3 * mm, "tangentPropagation" : true});
        }
    });
